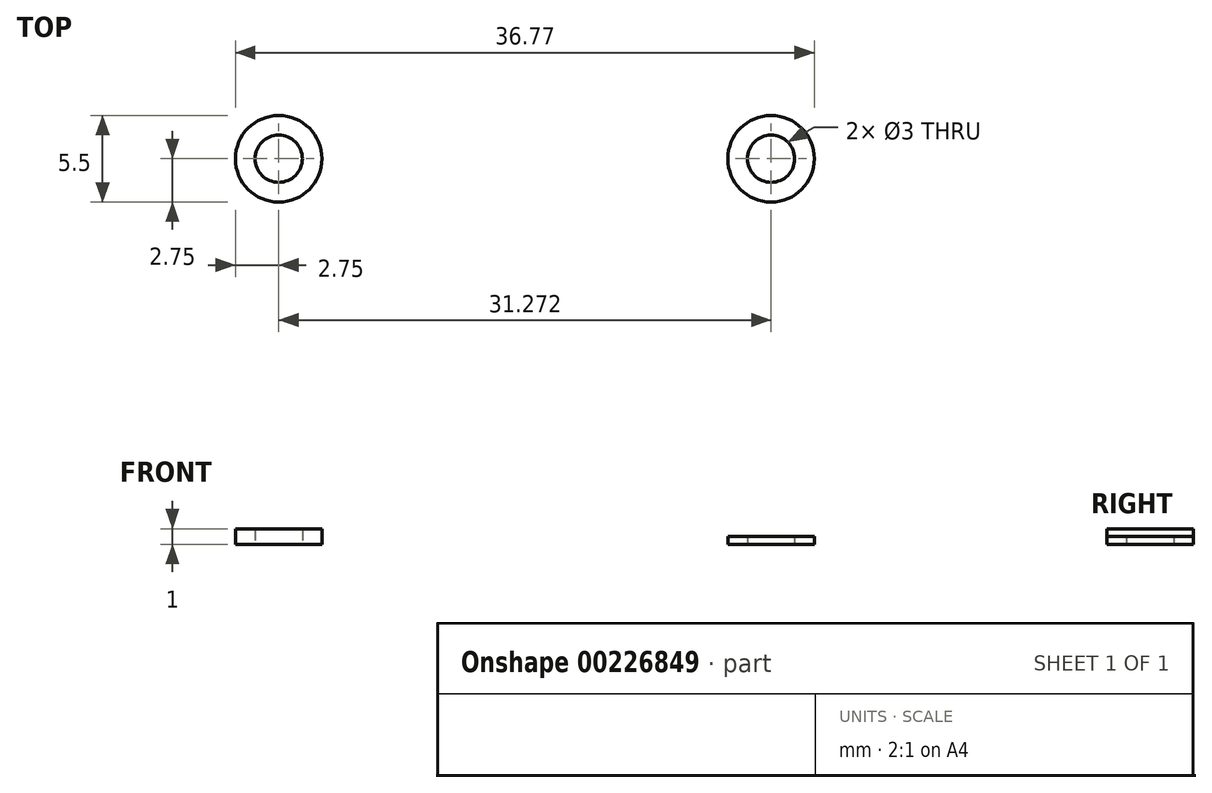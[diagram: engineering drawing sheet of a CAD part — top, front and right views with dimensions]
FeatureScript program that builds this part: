
annotation { "Feature Type Name" : "Feature", "Feature Type Description" : "" }
export const myFeature = defineFeature(function(context is Context, id is Id, definition is map)
    precondition{}
    {
        {
            var Q0;
            Q0=qCreatedBy(makeId("Top.planeOp"),FACE);
            var sketch = newSketch(context, id + "F0", { "sketchPlane" : qUnion([Q0])});
            skCircle(sketch, "E0", {"center": v(0, 0) * mm, "radius": 1.5 * mm});
            skCircle(sketch, "E1", {"center": v(0, 0) * mm, "radius": 2.75 * mm});
            skSolve(sketch);
        }
        {
            var Q0;
            Q0 = qSketchRegion(id + "F0", true);
            extrude(context, id + "F1", {"entities" : qUnion([Q0]), "depth" : 1 * mm});
        }
        {
            var Q0;
            Q0=qCreatedBy(makeId("Top.planeOp"),FACE);
            var sketch = newSketch(context, id + "F2", { "sketchPlane" : qUnion([Q0])});
            skCircle(sketch, "E2", {"center": v(31.27, 0) * mm, "radius": 1.5 * mm});
            skCircle(sketch, "E3", {"center": v(31.27, 0) * mm, "radius": 2.75 * mm});
            skSolve(sketch);
        }
        {
            var Q0;
            Q0 = qSketchRegion(id + "F2", true);
            extrude(context, id + "F3", {"entities" : qUnion([Q0]), "depth" : .5 * mm});
        }
    });
